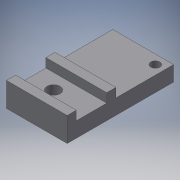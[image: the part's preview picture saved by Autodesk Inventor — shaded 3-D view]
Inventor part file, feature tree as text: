
AUTODESK INVENTOR PART (.ipt)
format: ipt  version: 2019 (Build 230136000, 136)  size: 144,384 bytes
history: native  units: in
note: dims shown in document units (in); Inventor stores cm internally (conversion verified against a paired STEP export)
features: sketch x5, extrude x4, hole x1, projected_geometry x1
ambient origin geometry x8: Origin, YZ Plane, XZ Plane, XY Plane, X Axis, Y Axis, Z Axis, Center Point
bodies: Solid1 (feature_tree)
feature tree (11):
  extrude  "Extrusion1"  Depth=0.7874in
  extrude  "Extrusion2"  Depth=0.1181in
  hole  "Hole1"  [1 undecoded]
  extrude  "Extrusion3"  Depth=0.1181in
  extrude  "Extrusion4"  Depth=0.1181in
  sketch  "Sketch1"  dims[d0=0.1969in d1=0.0in d2=0.7874in]
  sketch  "Sketch2"  dims[d3=1.378in d4=0.1181in]
  sketch  "Sketch3"  dims[d5=0.1181in d6=0.3937in]
  projected_geometry  "Projected Loop1"
  sketch  "Sketch4"  dims[d7=0.1181in d8=0.0in]
  sketch  "Sketch5"  dims[d9=0.1695in d10=0.2362in d11=0.279in d12=0.0787in d13=0.5635in d14=0.315in d15=0.8108in d16=0.3125in d17=0.6487in d18=0.1969in d19=0.0in d20=0.1181in d21=0.1181in d23=0.1969in d24=0.0in d25=0.1181in d26=0.4921in]
note: 1 required parameter value undecoded (feature->parameter linkage not recoverable at this tier; creation-order binding heuristic only, values carry confidence <= 0.55)
